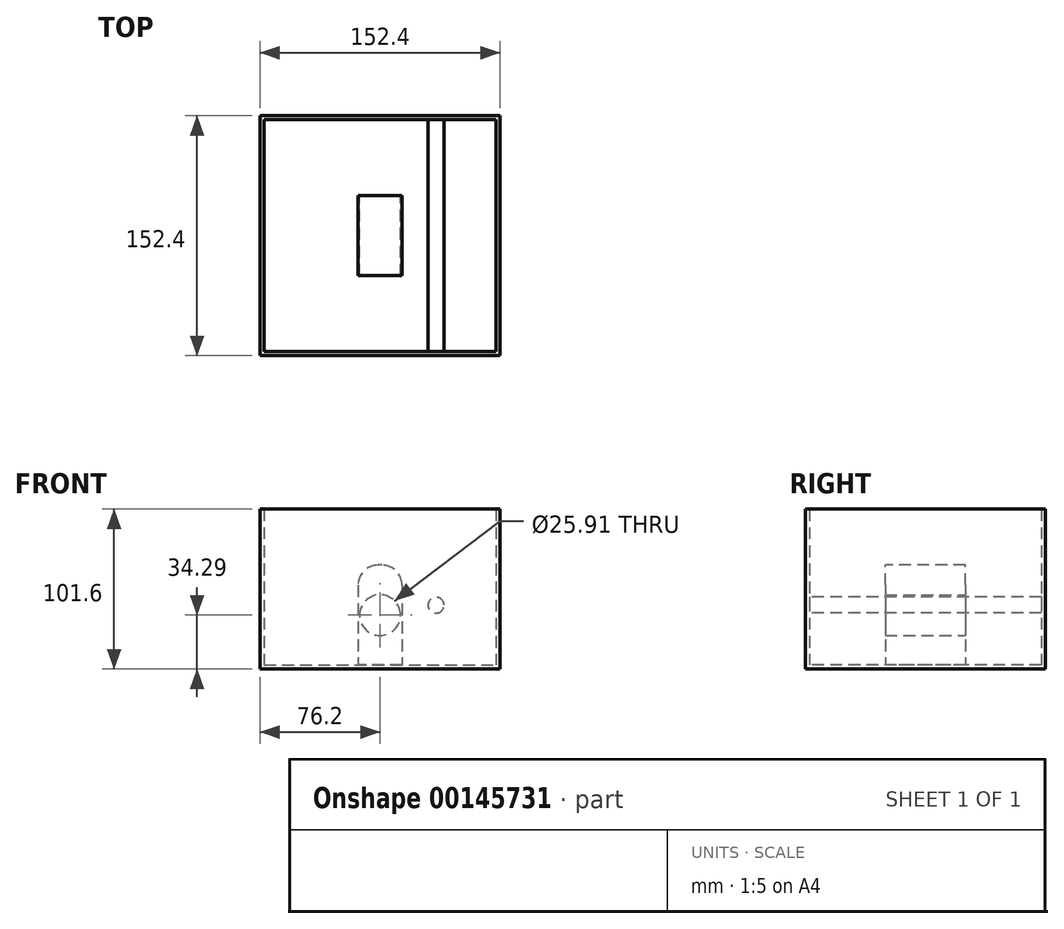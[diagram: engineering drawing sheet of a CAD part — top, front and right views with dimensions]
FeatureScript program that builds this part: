
annotation { "Feature Type Name" : "Feature", "Feature Type Description" : "" }
export const myFeature = defineFeature(function(context is Context, id is Id, definition is map)
    precondition{}
    {
        {
            var Q0;
            Q0=qCreatedBy(makeId("Top.planeOp"),FACE);
            var sketch = newSketch(context, id + "F0", { "sketchPlane" : qUnion([Q0])});
            skLineSegment(sketch, "E0.bottom", {"start": v(-76.2, 76.2) * mm, "end": v(76.2, 76.2) * mm});
            skLineSegment(sketch, "E0.top", {"start": v(-76.2, -76.2) * mm, "end": v(76.2, -76.2) * mm});
            skLineSegment(sketch, "E0.left", {"start": v(-76.2, 76.2) * mm, "end": v(-76.2, -76.2) * mm});
            skLineSegment(sketch, "E0.right", {"start": v(76.2, 76.2) * mm, "end": v(76.2, -76.2) * mm});
            skPoint(sketch, "E0.middle", {"position": v(0, 0) * mm});
            skSolve(sketch);
        }
        {
            var Q0;
            Q0 = qSketchRegion(id + "F0", true);
            extrude(context, id + "F1", {"entities" : qUnion([Q0]), "depth" : 101.6 * mm});
        }
        {
            var Q0;
            Q0=makeQuery(id+"F1.opExtrude","CAP_FACE",FACE,{"disambiguationData":[OSD([sQuery(id+"F0.wireOp",EDGE,"E0.bottom"),sQuery(id+"F0.wireOp",EDGE,"E0.top"),sQuery(id+"F0.wireOp",EDGE,"E0.left"),sQuery(id+"F0.wireOp",EDGE,"E0.right")])],"isStart":false});
            shell(context, id + "F2", {"entities" : qUnion([Q0]), "thickness" : 2.54 * mm});
        }
        {
            var Q0;
            Q0=makeQuery(id+"F2.opShell","OFFSET_FACE",FACE,{"disambiguationData":[OSD([sQuery(id+"F0.wireOp",EDGE,"E0.top")])]});
            var sketch = newSketch(context, id + "F3", { "sketchPlane" : qUnion([Q0])});
            skCircle(sketch, "E1", {"center": v(-35.56, 40.64) * mm, "radius": 5.08 * mm});
            skLineSegment(sketch, "E2", {"start": v(-35.56, 40.64) * mm, "end": v(-35.56, 2.54) * mm, "construction": true});
            skLineSegment(sketch, "E3", {"start": v(-35.56, 40.64) * mm, "end": v(-73.66, 40.64) * mm, "construction": true});
            skSolve(sketch);
        }
        {
            var Q0;
            Q0 = qSketchRegion(id + "F3", true);
            extrude(context, id + "F4", {"entities" : qUnion([Q0]), "operationType" : NewBodyOperationType.ADD, "depth" : 149.86 * mm});
        }
        {
            var Q0;
            Q0=makeQuery(id+"F2.opShell","OFFSET_FACE",FACE,{"disambiguationData":[OSD([sQuery(id+"F0.wireOp",EDGE,"E0.bottom"),sQuery(id+"F0.wireOp",EDGE,"E0.top"),sQuery(id+"F0.wireOp",EDGE,"E0.left"),sQuery(id+"F0.wireOp",EDGE,"E0.right")])]});
            var sketch = newSketch(context, id + "F5", { "sketchPlane" : qUnion([Q0])});
            skLineSegment(sketch, "E4.bottom", {"start": v(13.97, 25.4) * mm, "end": v(-13.97, 25.4) * mm});
            skLineSegment(sketch, "E4.top", {"start": v(13.97, -25.4) * mm, "end": v(-13.97, -25.4) * mm});
            skLineSegment(sketch, "E4.left", {"start": v(13.97, 25.4) * mm, "end": v(13.97, -25.4) * mm});
            skLineSegment(sketch, "E4.right", {"start": v(-13.97, 25.4) * mm, "end": v(-13.97, -25.4) * mm});
            skPoint(sketch, "E4.middle", {"position": v(0, 0) * mm});
            skSolve(sketch);
        }
        {
            var Q0;
            Q0 = qSketchRegion(id + "F5", true);
            extrude(context, id + "F6", {"entities" : qUnion([Q0]), "operationType" : NewBodyOperationType.ADD, "depth" : 63.5 * mm});
        }
        {
            var Q0;
            Q0=makeQuery(id+"F6.opExtrude","SWEPT_FACE",FACE,{"disambiguationData":[OSD([sQuery(id+"F5.wireOp",EDGE,"E4.bottom")])]});
            var sketch = newSketch(context, id + "F7", { "sketchPlane" : qUnion([Q0])});
            skCircle(sketch, "E5", {"center": v(0, 34.3) * mm, "radius": 12.95 * mm});
            skLineSegment(sketch, "E6", {"start": v(0, 34.3) * mm, "end": v(13.97, 66.04) * mm, "construction": true});
            skLineSegment(sketch, "E7", {"start": v(0, 34.3) * mm, "end": v(-13.97, 66.04) * mm, "construction": true});
            skLineSegment(sketch, "E8", {"start": v(0, 34.3) * mm, "end": v(13.97, 2.54) * mm, "construction": true});
            skLineSegment(sketch, "E9", {"start": v(0, 34.3) * mm, "end": v(-13.97, 2.54) * mm, "construction": true});
            skSolve(sketch);
        }
        {
            var Q0;
            Q0 = qSketchRegion(id + "F7", true);
            extrude(context, id + "F8", {"entities" : qUnion([Q0]), "operationType" : NewBodyOperationType.REMOVE, "oppositeDirection" : true, "depth" : 50.8 * mm});
        }
        {
            var Q0;
            Q0=makeQuery(id+"F6.opExtrude","CAP_EDGE",EDGE,{"disambiguationData":[OSD([sQuery(id+"F5.wireOp",EDGE,"E4.right")])],"isStart":false});
            fillet(context, id + "F9", {"entities" : qUnion([Q0]), "radius" : 12.7 * mm, "tangentPropagation" : true, "allowEdgeOverflow" : false});
        }
        {
            var Q0;
            Q0=makeQuery(id+"F6.opExtrude","CAP_EDGE",EDGE,{"disambiguationData":[OSD([sQuery(id+"F5.wireOp",EDGE,"E4.left")])],"isStart":false});
            fillet(context, id + "F10", {"entities" : qUnion([Q0]), "radius" : 12.7 * mm, "tangentPropagation" : true, "allowEdgeOverflow" : false});
        }
    });
